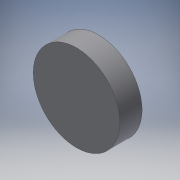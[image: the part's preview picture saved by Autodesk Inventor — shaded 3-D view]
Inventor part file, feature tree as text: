
AUTODESK INVENTOR PART (.ipt)
format: ipt  version: 2016 SP2 (Build 200236200, 236)  size: 98,816 bytes
history: native  units: mm
features: extrude x2, sketch x2
ambient origin geometry x8: Origin, YZ Plane, XZ Plane, XY Plane, X Axis, Y Axis, Z Axis, Center Point
bodies: Volumenkörper1 (feature_tree)
feature tree (4):
  extrude  "Extrusion1"  Depth=3.8mm TaperAngle=0.0deg
  extrude  "Extrusion2"  Depth=0.8mm TaperAngle=0.0deg
  sketch  "Skizze1"  dims[d0=14.8mm d1=3.8mm d2=0.0mm]
  sketch  "Skizze2"  dims[d3=11.8mm d4=0.8mm d5=0.0mm]
